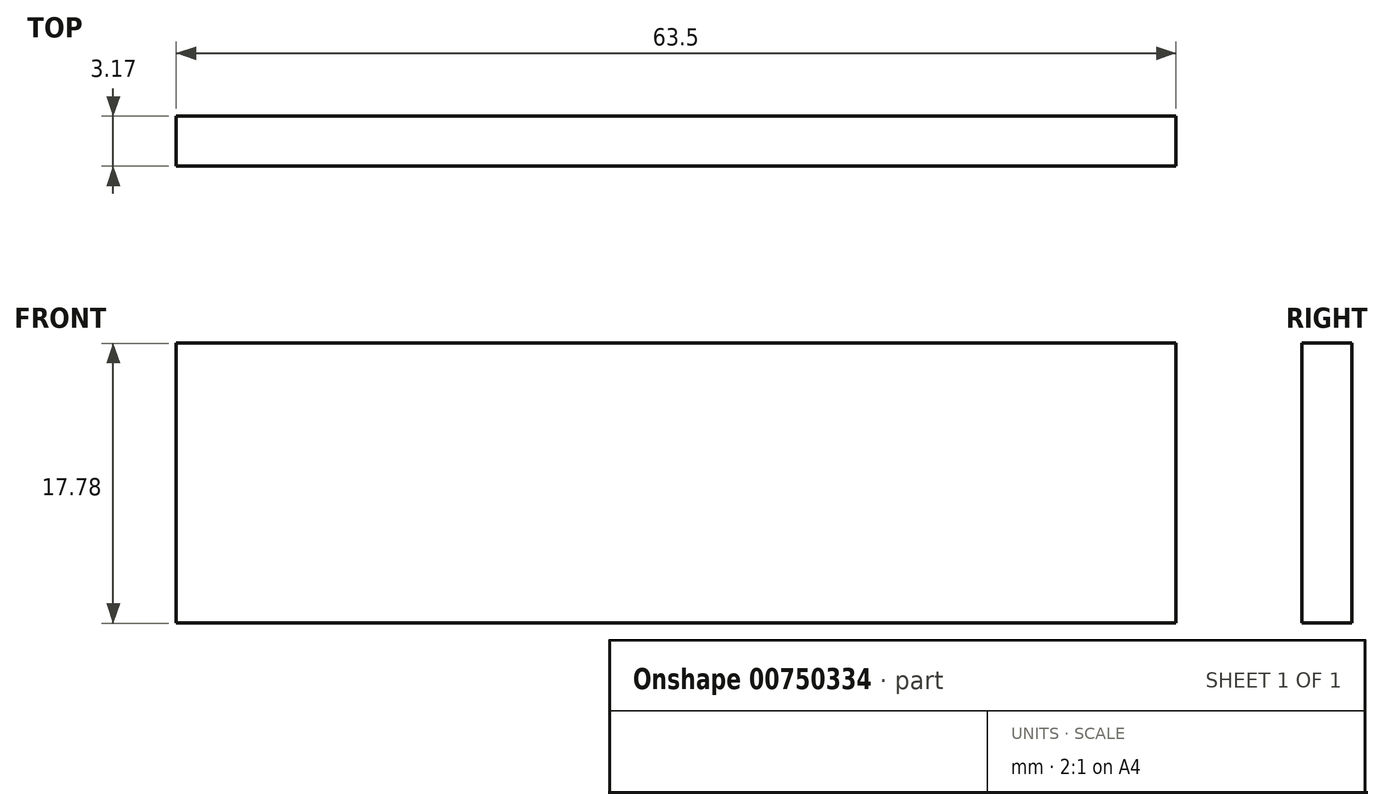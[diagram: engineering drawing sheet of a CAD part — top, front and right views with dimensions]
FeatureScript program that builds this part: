
annotation { "Feature Type Name" : "Feature", "Feature Type Description" : "" }
export const myFeature = defineFeature(function(context is Context, id is Id, definition is map)
    precondition{}
    {
        {
            var Q0;
            Q0=qCreatedBy(makeId("Front.planeOp"),FACE);
            var sketch = newSketch(context, id + "F0", { "sketchPlane" : qUnion([Q0])});
            skLineSegment(sketch, "E0.bottom", {"start": v(-19.38, 7.56) * mm, "end": v(44.12, 7.56) * mm});
            skLineSegment(sketch, "E0.top", {"start": v(-19.38, -10.22) * mm, "end": v(44.12, -10.22) * mm});
            skLineSegment(sketch, "E0.left", {"start": v(-19.38, 7.56) * mm, "end": v(-19.38, -10.22) * mm});
            skLineSegment(sketch, "E0.right", {"start": v(44.12, 7.56) * mm, "end": v(44.12, -10.22) * mm});
            skSolve(sketch);
        }
        {
            var Q0;
            Q0 = qSketchRegion(id + "F0", true);
            extrude(context, id + "F1", {"entities" : qUnion([Q0]), "depth" : 3.17 * mm, "offsetDistance" : 25.4 * mm});
        }
    });
